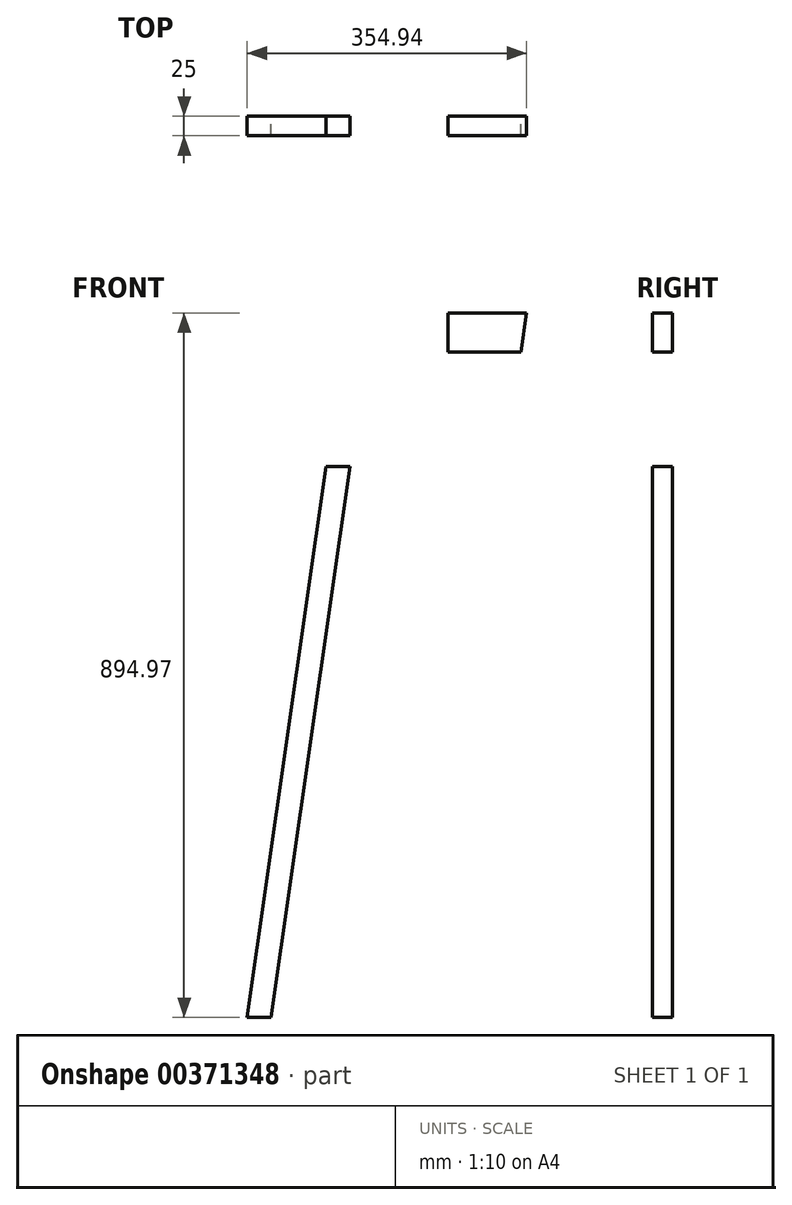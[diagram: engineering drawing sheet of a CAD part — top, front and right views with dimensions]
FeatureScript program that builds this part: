
annotation { "Feature Type Name" : "Feature", "Feature Type Description" : "" }
export const myFeature = defineFeature(function(context is Context, id is Id, definition is map)
    precondition{}
    {
        {
            var Q0;
            Q0=qCreatedBy(makeId("Front.planeOp"),FACE);
            var sketch = newSketch(context, id + "F0", { "sketchPlane" : qUnion([Q0])});
            skLineSegment(sketch, "E0", {"start": v(0, 0) * mm, "end": v(0, 700) * mm, "construction": true});
            skLineSegment(sketch, "E1", {"start": v(0, 700) * mm, "end": v(50, 700) * mm, "construction": true});
            skLineSegment(sketch, "E2", {"start": v(50, 700) * mm, "end": v(50, 0) * mm, "construction": true});
            skLineSegment(sketch, "E3", {"start": v(50, 700) * mm, "end": v(150, 700) * mm, "construction": true});
            skLineSegment(sketch, "E4", {"start": v(150, 700) * mm, "end": v(50, 0) * mm, "construction": true});
            skLineSegment(sketch, "E5", {"start": v(150, 700) * mm, "end": v(179.7, 695.76) * mm, "construction": true});
            skLineSegment(sketch, "E6", {"start": v(179.7, 695.76) * mm, "end": v(79.7, -4.24) * mm, "construction": true});
            skLineSegment(sketch, "E7", {"start": v(50, 0) * mm, "end": v(79.7, -4.24) * mm, "construction": true});
            skLineSegment(sketch, "E8", {"start": v(150, 700) * mm, "end": v(190.85, 700) * mm, "construction": true});
            skLineSegment(sketch, "E9", {"start": v(179.7, 695.76) * mm, "end": v(180.3, 700) * mm, "construction": true});
            skLineSegment(sketch, "E10", {"start": v(150, 700) * mm, "end": v(150.6, 704.24) * mm, "construction": true});
            skLineSegment(sketch, "E11", {"start": v(180.3, 700) * mm, "end": v(150.6, 704.24) * mm, "construction": true});
            skLineSegment(sketch, "E12", {"start": v(50, 700) * mm, "end": v(50, 650) * mm, "construction": true});
            skLineSegment(sketch, "E13", {"start": v(50, 650) * mm, "end": v(142.86, 650) * mm, "construction": true});
            skLineSegment(sketch, "E14", {"start": v(50, 700) * mm, "end": v(50, 650) * mm});
            skLineSegment(sketch, "E15", {"start": v(150, 700) * mm, "end": v(50, 700) * mm});
            skLineSegment(sketch, "E16", {"start": v(50, 650) * mm, "end": v(142.86, 650) * mm});
            skLineSegment(sketch, "E17", {"start": v(150, 700) * mm, "end": v(142.86, 650) * mm});
            skLineSegment(sketch, "E18", {"start": v(-215.54, 664.9) * mm, "end": v(-215.54, 614.9) * mm});
            skLineSegment(sketch, "E19", {"start": v(-115.54, 664.9) * mm, "end": v(-215.54, 664.9) * mm});
            skLineSegment(sketch, "E20", {"start": v(-215.54, 614.9) * mm, "end": v(-122.68, 614.9) * mm});
            skLineSegment(sketch, "E21", {"start": v(-115.54, 664.9) * mm, "end": v(-122.68, 614.9) * mm});
            skLineSegment(sketch, "E22", {"start": v(50, 0) * mm, "end": v(80.3, 0) * mm});
            skLineSegment(sketch, "E23", {"start": v(80.3, 0) * mm, "end": v(180.3, 700) * mm});
            skLineSegment(sketch, "E24", {"start": v(180.3, 700) * mm, "end": v(150, 700) * mm});
            skLineSegment(sketch, "E25", {"start": v(50, 0) * mm, "end": v(150, 700) * mm});
            skLineSegment(sketch, "E26", {"start": v(-470.48, -230.08) * mm, "end": v(-440.18, -230.08) * mm});
            skLineSegment(sketch, "E27", {"start": v(-440.18, -230.08) * mm, "end": v(-340.18, 469.92) * mm});
            skLineSegment(sketch, "E28", {"start": v(-340.18, 469.92) * mm, "end": v(-370.48, 469.92) * mm});
            skLineSegment(sketch, "E29", {"start": v(-470.48, -230.08) * mm, "end": v(-370.48, 469.92) * mm});
            skSolve(sketch);
        }
        {
            var Q0;
            Q0=makeQuery(id+"F0.imprint","IMPRINT",FACE,{"disambiguationData":[TD([[makeQuery(id+"F0.imprint","IMPRINT",EDGE,{"derivedFrom":sQuery(id+"F0.wireOp",EDGE,"E26")}),1.0]])]});
            var Q1;
            Q1=makeQuery(id+"F0.imprint","IMPRINT",FACE,{"disambiguationData":[TD([[makeQuery(id+"F0.imprint","IMPRINT",EDGE,{"derivedFrom":sQuery(id+"F0.wireOp",EDGE,"E18")}),1.0]])]});
            extrude(context, id + "F1", {"entities" : qUnion([Q0, Q1]), "depth" : 25 * mm});
        }
    });
